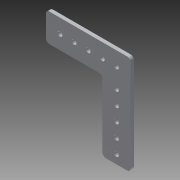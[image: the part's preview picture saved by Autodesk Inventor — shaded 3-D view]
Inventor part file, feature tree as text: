
AUTODESK INVENTOR PART (.ipt)
format: ipt  version: 2014 (Build 180170000, 170)  size: 112,640 bytes
history: native  units: in
note: dims shown in document units (in); Inventor stores cm internally (conversion verified against a paired STEP export)
features: extrude x1, fillet x1, sketch x1
ambient origin geometry x8: Origin, YZ Plane, XZ Plane, XY Plane, X Axis, Y Axis, Z Axis, Center Point
bodies: Solid1 (feature_tree)
feature tree (3):
  extrude  "Extrusion1"  Depth=1.0in
  fillet  "Fillet1"  Radius=3.5in
  sketch  "Sketch1"  dims[d0=3.0in d3=1.0in d4=3.5in d5=0.163in d6=0.5in d7=0.5in d16=1.9685in d18=0.5in d19=0.3937in d21=1.0in d23=0.5in d24=0.125in d25=0.0in d26=0.125in d27=0.1875in d28=1.0in d29=1.9685in d31=0.5in d32=0.3937in d34=1.0in]
